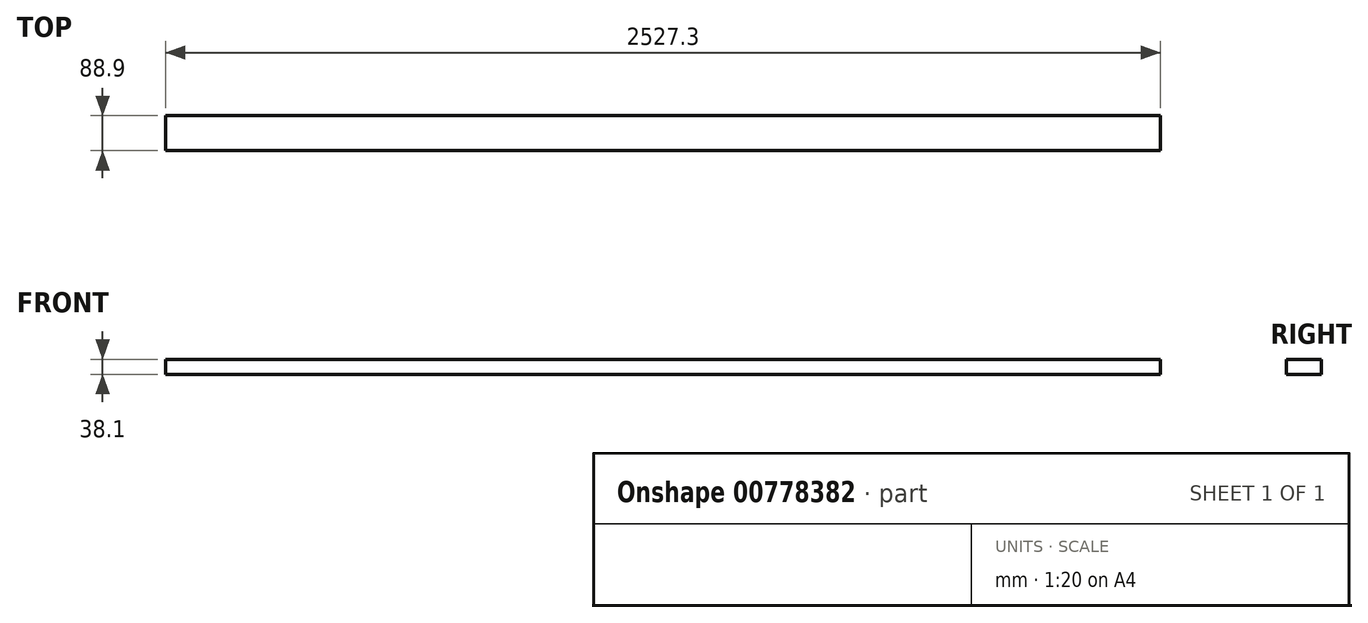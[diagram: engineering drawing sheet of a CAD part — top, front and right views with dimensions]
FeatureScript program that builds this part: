
annotation { "Feature Type Name" : "Feature", "Feature Type Description" : "" }
export const myFeature = defineFeature(function(context is Context, id is Id, definition is map)
    precondition{}
    {
        {
            var Q0;
            Q0=qCreatedBy(makeId("Front.planeOp"),FACE);
            var sketch = newSketch(context, id + "F0", { "sketchPlane" : qUnion([Q0])});
            skLineSegment(sketch, "E0.bottom", {"start": v(0, 0) * mm, "end": v(2527.3, 0) * mm});
            skLineSegment(sketch, "E0.top", {"start": v(0, 38.1) * mm, "end": v(2527.3, 38.1) * mm});
            skLineSegment(sketch, "E0.left", {"start": v(0, 0) * mm, "end": v(0, 38.1) * mm});
            skLineSegment(sketch, "E0.right", {"start": v(2527.3, 0) * mm, "end": v(2527.3, 38.1) * mm});
            skSolve(sketch);
        }
        {
            var Q0;
            Q0 = qSketchRegion(id + "F0", true);
            extrude(context, id + "F1", {"entities" : qUnion([Q0]), "depth" : 88.9 * mm, "offsetDistance" : 25.4 * mm});
        }
    });
